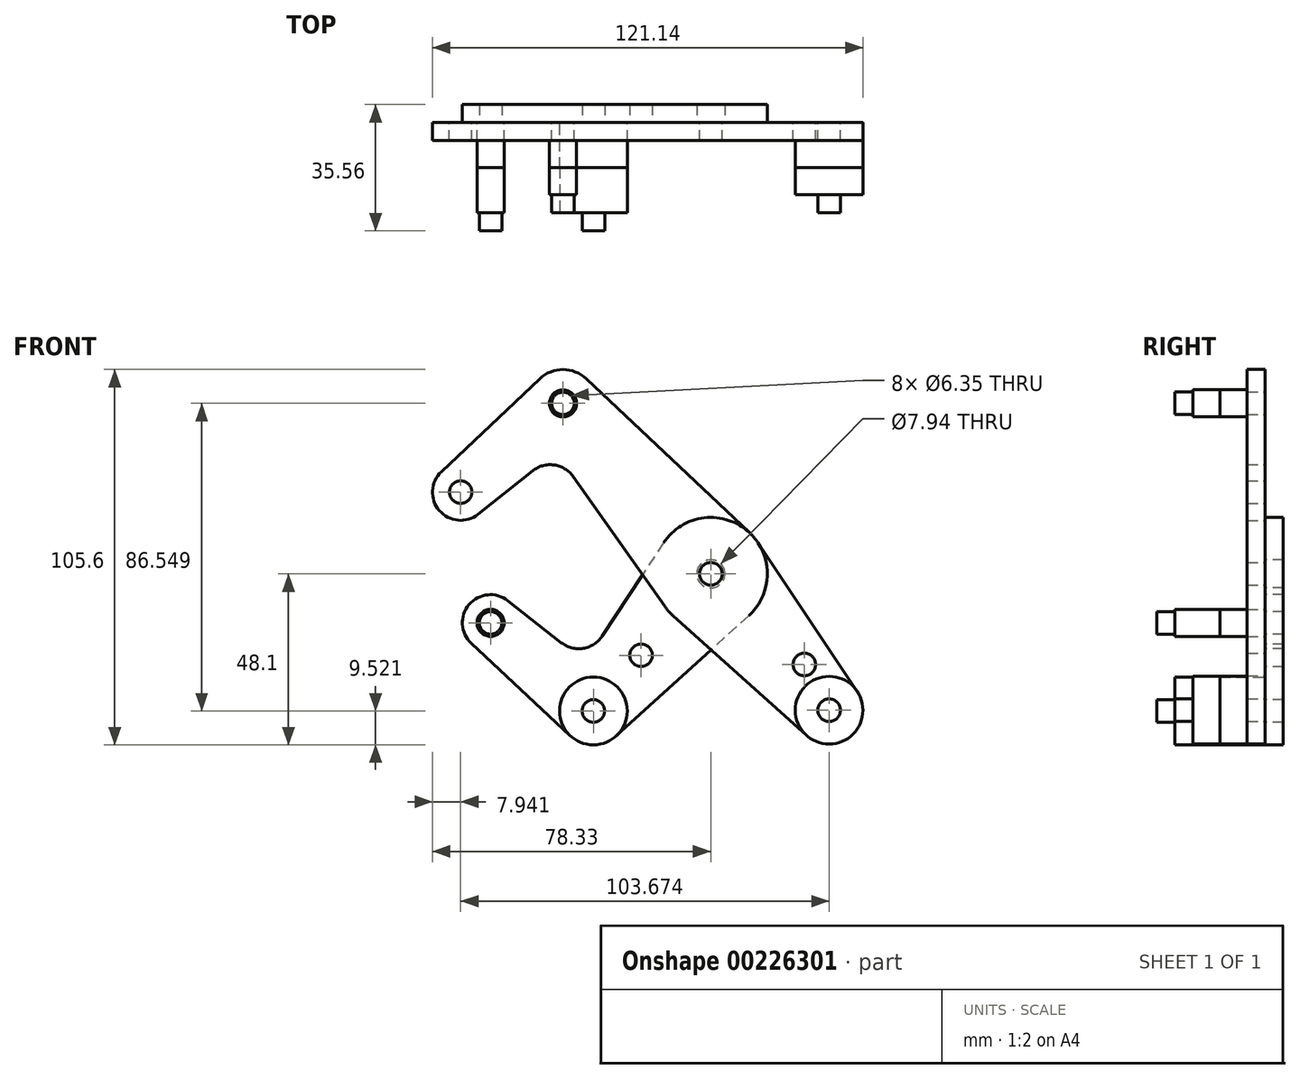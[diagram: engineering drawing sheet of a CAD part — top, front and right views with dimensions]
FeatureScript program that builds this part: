
annotation { "Feature Type Name" : "Feature", "Feature Type Description" : "" }
export const myFeature = defineFeature(function(context is Context, id is Id, definition is map)
    precondition{}
    {
        {
            var Q0;
            Q0=qCreatedBy(makeId("Front.planeOp"),FACE);
            var sketch = newSketch(context, id + "F0", { "sketchPlane" : qUnion([Q0])});
            skLineSegment(sketch, "E0", {"start": v(-41.6, 47.97) * mm, "end": v(41.6, -47.97) * mm, "construction": true});
            skCircle(sketch, "E1", {"center": v(0, 0) * mm, "radius": 3.18 * mm});
            skCircle(sketch, "E2", {"center": v(33.29, -38.38) * mm, "radius": 3.18 * mm});
            skCircle(sketch, "E3", {"center": v(-41.6, 47.97) * mm, "radius": 3.18 * mm});
            skCircle(sketch, "E4", {"center": v(-70.39, 23) * mm, "radius": 3.18 * mm});
            skLineSegment(sketch, "E5", {"start": v(-41.6, 47.97) * mm, "end": v(-70.39, 23) * mm, "construction": true});
            skCircle(sketch, "E6", {"center": v(33.29, -38.38) * mm, "radius": 9.53 * mm});
            skCircle(sketch, "E7", {"center": v(-70.39, 23) * mm, "radius": 7.94 * mm});
            skCircle(sketch, "E8", {"center": v(-41.6, 47.97) * mm, "radius": 9.53 * mm});
            skLineSegment(sketch, "E9", {"start": v(-75.83, 28.78) * mm, "end": v(-48.14, 54.9) * mm});
            skLineSegment(sketch, "E10", {"start": v(-65.44, 16.8) * mm, "end": v(-50.15, 28.98) * mm});
            skCircle(sketch, "E11", {"center": v(0, 0) * mm, "radius": 15.88 * mm});
            skLineSegment(sketch, "E12", {"start": v(-35.07, 54.9) * mm, "end": v(10.9, 11.55) * mm});
            skLineSegment(sketch, "E13", {"start": v(-38.72, 27.35) * mm, "end": v(-12.97, -9.15) * mm});
            skLineSegment(sketch, "E14", {"start": v(-10.6, -11.82) * mm, "end": v(26.93, -45.47) * mm});
            skLineSegment(sketch, "E15", {"start": v(13.2, 8.82) * mm, "end": v(41.2, -33.08) * mm});
            skArc(sketch, "E16.filletArc", {"start": v(-38.72, 27.35) * mm, "mid": v(-44.08, 30.63) * mm, "end": v(-50.15, 28.98) * mm});
            skLineSegment(sketch, "E17", {"start": v(0, 0) * mm, "end": v(-33.05, -38.58) * mm, "construction": true});
            skLineSegment(sketch, "E18", {"start": v(-33.05, -38.58) * mm, "end": v(-61.98, -13.8) * mm, "construction": true});
            skCircle(sketch, "E19", {"center": v(-61.98, -13.8) * mm, "radius": 3.18 * mm});
            skCircle(sketch, "E20", {"center": v(-33.05, -38.58) * mm, "radius": 3.18 * mm});
            skCircle(sketch, "E21", {"center": v(-61.98, -13.8) * mm, "radius": 7.94 * mm});
            skCircle(sketch, "E22", {"center": v(-33.05, -38.58) * mm, "radius": 9.53 * mm});
            skLineSegment(sketch, "E23", {"start": v(-57.08, -7.55) * mm, "end": v(-42.08, -19.35) * mm});
            skLineSegment(sketch, "E24", {"start": v(-67.4, -19.6) * mm, "end": v(-39.54, -45.55) * mm});
            skLineSegment(sketch, "E25", {"start": v(-13.25, 8.74) * mm, "end": v(-30.55, -17.48) * mm});
            skLineSegment(sketch, "E26", {"start": v(10.67, -11.75) * mm, "end": v(-26.65, -45.63) * mm});
            skArc(sketch, "E27.filletArc", {"start": v(-42.08, -19.35) * mm, "mid": v(-35.9, -20.95) * mm, "end": v(-30.55, -17.48) * mm});
            skCircle(sketch, "E28", {"center": v(-19.62, -22.9) * mm, "radius": 3.18 * mm});
            skCircle(sketch, "E29", {"center": v(26.32, -25.5) * mm, "radius": 3.18 * mm});
            skLineSegment(sketch, "E30", {"start": v(26.32, -25.5) * mm, "end": v(23.92, -27.58) * mm, "construction": true});
            skCircle(sketch, "E31", {"center": v(0, 0) * mm, "radius": 3.97 * mm});
            skSolve(sketch);
        }
        {
            var Q0;
            Q0=qCreatedBy(makeId("Front.planeOp"),FACE);
            cPlane(context, id + "F1", {"entities" : qUnion([Q0]), "cplaneType" : CPlaneType.OFFSET, "offset" : 12.7 * mm, "width" : 254 * mm, "height" : 254 * mm});
        }
        {
            var Q0;
            Q0=makeQuery(id+"F0.imprint","IMPRINT",FACE,{"disambiguationData":[TD([[makeQuery(id+"F0.imprint","IMPRINT",EDGE,{"derivedFrom":sQuery(id+"F0.wireOp",EDGE,"E4")}),-1.0]])]});
            var Q1;
            {var subQ1=sQuery(id+"F0.wireOp",EDGE,"E9");Q1=makeQuery(id+"F0.imprint","IMPRINT",FACE,{"disambiguationData":[TD([[makeQuery(id+"F0.imprint","IMPRINT",EDGE,{"derivedFrom":subQ1}),-1.0]])]});}
            var Q2;
            Q2=makeQuery(id+"F0.imprint","IMPRINT",FACE,{"disambiguationData":[TD([[makeQuery(id+"F0.imprint","IMPRINT",EDGE,{"derivedFrom":sQuery(id+"F0.wireOp",EDGE,"E3")}),-1.0]])]});
            var Q3;
            Q3=makeQuery(id+"F0.imprint","IMPRINT",FACE,{"disambiguationData":[TD([[makeQuery(id+"F0.imprint","IMPRINT",EDGE,{"derivedFrom":sQuery(id+"F0.wireOp",EDGE,"E31")}),-1.0]])]});
            var Q4;
            {var subQ0=sQuery(id+"F0.wireOp",EDGE,"E13");var subQ1=sQuery(id+"F0.wireOp",EDGE,"E11");var subQ2=makeQuery(id+"F0.imprint","INTERSECT",VERTEX,{"derivedFrom":[subQ1,subQ0]});Q4=makeQuery(id+"F0.imprint","IMPRINT",FACE,{"disambiguationData":[TD([[makeQuery(id+"F0.imprint","IMPRINT",EDGE,{"disambiguationData":[TD([[subQ2,1.0]])],"derivedFrom":subQ1}),-1.0]])]});}
            var Q5;
            {var subQ0=sQuery(id+"F0.wireOp",EDGE,"E14");var subQ1=sQuery(id+"F0.wireOp",EDGE,"E11");var subQ2=makeQuery(id+"F0.imprint","INTERSECT",VERTEX,{"derivedFrom":[subQ1,subQ0]});Q5=makeQuery(id+"F0.imprint","IMPRINT",FACE,{"disambiguationData":[TD([[makeQuery(id+"F0.imprint","IMPRINT",EDGE,{"disambiguationData":[TD([[subQ2,-1.0]])],"derivedFrom":subQ1}),-1.0]])]});}
            var Q6;
            {var subQ0=sQuery(id+"F0.wireOp",EDGE,"E15");Q6=makeQuery(id+"F0.imprint","IMPRINT",FACE,{"disambiguationData":[TD([[makeQuery(id+"F0.imprint","IMPRINT",EDGE,{"derivedFrom":subQ0}),-1.0]])]});}
            var Q7;
            Q7=makeQuery(id+"F0.imprint","IMPRINT",FACE,{"disambiguationData":[TD([[makeQuery(id+"F0.imprint","IMPRINT",EDGE,{"derivedFrom":sQuery(id+"F0.wireOp",EDGE,"E2")}),-1.0]])]});
            var Q8;
            Q8=makeQuery(id+"F0.imprint","IMPRINT",FACE,{"disambiguationData":[TD([[makeQuery(id+"F0.imprint","IMPRINT",EDGE,{"derivedFrom":sQuery(id+"F0.wireOp",EDGE,"E1")}),-1.0]])]});
            extrude(context, id + "F2", {"entities" : qUnion([Q0, Q1, Q2, Q3, Q4, Q5, Q6, Q7, Q8]), "depth" : 5.08 * mm});
        }
        {
            var Q0;
            Q0=makeQuery(id+"F0.imprint","IMPRINT",FACE,{"disambiguationData":[TD([[makeQuery(id+"F0.imprint","IMPRINT",EDGE,{"derivedFrom":sQuery(id+"F0.wireOp",EDGE,"E31")}),-1.0]])]});
            var Q1;
            {var subQ0=sQuery(id+"F0.wireOp",EDGE,"E14");var subQ1=sQuery(id+"F0.wireOp",EDGE,"E11");var subQ2=makeQuery(id+"F0.imprint","INTERSECT",VERTEX,{"derivedFrom":[subQ1,subQ0]});Q1=makeQuery(id+"F0.imprint","IMPRINT",FACE,{"disambiguationData":[TD([[makeQuery(id+"F0.imprint","IMPRINT",EDGE,{"disambiguationData":[TD([[subQ2,-1.0]])],"derivedFrom":subQ1}),-1.0]])]});}
            var Q2;
            {var subQ10=sQuery(id+"F0.wireOp",EDGE,"E23");Q2=makeQuery(id+"F0.imprint","IMPRINT",FACE,{"disambiguationData":[TD([[makeQuery(id+"F0.imprint","IMPRINT",EDGE,{"derivedFrom":subQ10}),-1.0]])]});}
            var Q3;
            {var subQ0=sQuery(id+"F0.wireOp",EDGE,"E13");var subQ1=sQuery(id+"F0.wireOp",EDGE,"E11");var subQ2=makeQuery(id+"F0.imprint","INTERSECT",VERTEX,{"derivedFrom":[subQ1,subQ0]});Q3=makeQuery(id+"F0.imprint","IMPRINT",FACE,{"disambiguationData":[TD([[makeQuery(id+"F0.imprint","IMPRINT",EDGE,{"disambiguationData":[TD([[subQ2,1.0]])],"derivedFrom":subQ1}),-1.0]])]});}
            var Q4;
            Q4=makeQuery(id+"F0.imprint","IMPRINT",FACE,{"disambiguationData":[TD([[makeQuery(id+"F0.imprint","IMPRINT",EDGE,{"derivedFrom":sQuery(id+"F0.wireOp",EDGE,"E19")}),-1.0]])]});
            var Q5;
            Q5=makeQuery(id+"F0.imprint","IMPRINT",FACE,{"disambiguationData":[TD([[makeQuery(id+"F0.imprint","IMPRINT",EDGE,{"derivedFrom":sQuery(id+"F0.wireOp",EDGE,"E20")}),-1.0]])]});
            extrude(context, id + "F3", {"entities" : qUnion([Q0, Q1, Q2, Q3, Q4, Q5]), "oppositeDirection" : true, "depth" : 5.08 * mm});
        }
        {
            var Q0;
            Q0=makeQuery(id+"F2.opExtrude","CAP_FACE",FACE,{"disambiguationData":[OSD([sQuery(id+"F0.wireOp",EDGE,"E1"),sQuery(id+"F0.wireOp",EDGE,"E2"),sQuery(id+"F0.wireOp",EDGE,"E3"),sQuery(id+"F0.wireOp",EDGE,"E4"),sQuery(id+"F0.wireOp",EDGE,"E6"),sQuery(id+"F0.wireOp",EDGE,"E7"),sQuery(id+"F0.wireOp",EDGE,"E8"),sQuery(id+"F0.wireOp",EDGE,"E9"),sQuery(id+"F0.wireOp",EDGE,"E10"),sQuery(id+"F0.wireOp",EDGE,"E11"),sQuery(id+"F0.wireOp",EDGE,"E12"),sQuery(id+"F0.wireOp",EDGE,"E13"),sQuery(id+"F0.wireOp",EDGE,"E14"),sQuery(id+"F0.wireOp",EDGE,"E15"),sQuery(id+"F0.wireOp",EDGE,"E16.filletArc"),sQuery(id+"F0.wireOp",EDGE,"E29")])],"isStart":true});
            var sketch = newSketch(context, id + "F4", { "sketchPlane" : qUnion([Q0])});
            skCircle(sketch, "E32", {"center": v(41.6, 47.97) * mm, "radius": 3.81 * mm});
            skCircle(sketch, "E33.0", {"center": v(-33.29, -38.38) * mm, "radius": 9.53 * mm});
            skSolve(sketch);
        }
        {
            var Q0;
            Q0=makeQuery(id+"F3.opExtrude","CAP_FACE",FACE,{"disambiguationData":[OSD([sQuery(id+"F0.wireOp",EDGE,"E11"),sQuery(id+"F0.wireOp",EDGE,"E19"),sQuery(id+"F0.wireOp",EDGE,"E20"),sQuery(id+"F0.wireOp",EDGE,"E21"),sQuery(id+"F0.wireOp",EDGE,"E22"),sQuery(id+"F0.wireOp",EDGE,"E23"),sQuery(id+"F0.wireOp",EDGE,"E24"),sQuery(id+"F0.wireOp",EDGE,"E25"),sQuery(id+"F0.wireOp",EDGE,"E26"),sQuery(id+"F0.wireOp",EDGE,"E27.filletArc"),sQuery(id+"F0.wireOp",EDGE,"E28"),sQuery(id+"F0.wireOp",EDGE,"E31")])],"isStart":false});
            var sketch = newSketch(context, id + "F5", { "sketchPlane" : qUnion([Q0])});
            skCircle(sketch, "E34", {"center": v(61.98, -13.8) * mm, "radius": 3.81 * mm});
            skCircle(sketch, "E35.0", {"center": v(33.05, -38.58) * mm, "radius": 9.53 * mm});
            skSolve(sketch);
        }
        {
            var Q0;
            Q0 = qSketchRegion(id + "F4", true);
            var Q1;
            Q1 = qSketchRegion(id + "F5", true);
            var Q2;
            Q2=qCreatedBy(id+"F1.planeOp",FACE);
            extrude(context, id + "F6", {"entities" : qUnion([Q0, Q1]), "endBound" : BoundingType.UP_TO_SURFACE, "oppositeDirection" : true, "endBoundEntityFace" : qUnion([Q2]), "depth" : 25.4 * mm});
        }
        {
            var Q0;
            Q0=makeQuery(id+"F2.opExtrude","SWEPT_BODY",BODY,{"disambiguationData":[OSD([sQuery(id+"F0.wireOp",EDGE,"E1"),sQuery(id+"F0.wireOp",EDGE,"E2"),sQuery(id+"F0.wireOp",EDGE,"E3"),sQuery(id+"F0.wireOp",EDGE,"E4"),sQuery(id+"F0.wireOp",EDGE,"E6"),sQuery(id+"F0.wireOp",EDGE,"E7"),sQuery(id+"F0.wireOp",EDGE,"E8"),sQuery(id+"F0.wireOp",EDGE,"E9"),sQuery(id+"F0.wireOp",EDGE,"E10"),sQuery(id+"F0.wireOp",EDGE,"E11"),sQuery(id+"F0.wireOp",EDGE,"E12"),sQuery(id+"F0.wireOp",EDGE,"E13"),sQuery(id+"F0.wireOp",EDGE,"E14"),sQuery(id+"F0.wireOp",EDGE,"E15"),sQuery(id+"F0.wireOp",EDGE,"E16.filletArc"),sQuery(id+"F0.wireOp",EDGE,"E29")])]});
            var Q1;
            Q1=makeQuery(id+"F3.opExtrude","SWEPT_BODY",BODY,{"disambiguationData":[OSD([sQuery(id+"F0.wireOp",EDGE,"E11"),sQuery(id+"F0.wireOp",EDGE,"E19"),sQuery(id+"F0.wireOp",EDGE,"E20"),sQuery(id+"F0.wireOp",EDGE,"E21"),sQuery(id+"F0.wireOp",EDGE,"E22"),sQuery(id+"F0.wireOp",EDGE,"E23"),sQuery(id+"F0.wireOp",EDGE,"E24"),sQuery(id+"F0.wireOp",EDGE,"E25"),sQuery(id+"F0.wireOp",EDGE,"E26"),sQuery(id+"F0.wireOp",EDGE,"E27.filletArc"),sQuery(id+"F0.wireOp",EDGE,"E28"),sQuery(id+"F0.wireOp",EDGE,"E31")])]});
            var Q2;
            Q2=makeQuery(id+"F6.opExtrude","SWEPT_BODY",BODY,{"disambiguationData":[OSD([sQuery(id+"F4.wireOp",EDGE,"E32")])]});
            var Q3;
            Q3=makeQuery(id+"F6.opExtrude","SWEPT_BODY",BODY,{"disambiguationData":[OSD([sQuery(id+"F5.wireOp",EDGE,"E34")])]});
            var Q4;
            Q4=makeQuery(id+"F6.opExtrude","SWEPT_BODY",BODY,{"disambiguationData":[OSD([sQuery(id+"F5.wireOp",EDGE,"E35.0")])]});
            var Q5;
            Q5=makeQuery(id+"F6.opExtrude","SWEPT_BODY",BODY,{"disambiguationData":[OSD([sQuery(id+"F4.wireOp",EDGE,"E33.0")])]});
            booleanBodies(context, id + "F7", {"operationType" : BooleanOperationType.SUBTRACTION, "tools" : qUnion([Q0, Q1]), "targets" : qUnion([Q2, Q3, Q4, Q5]), "keepTools" : true});
        }
        {
            var Q0;
            Q0=makeQuery(id+"F6.opExtrude","SWEPT_BODY",BODY,{"disambiguationData":[OSD([sQuery(id+"F5.wireOp",EDGE,"E35.0")])]});
            var Q1;
            Q1=makeQuery(id+"F6.opExtrude","SWEPT_BODY",BODY,{"disambiguationData":[OSD([sQuery(id+"F4.wireOp",EDGE,"E32")])]});
            var Q2;
            Q2=makeQuery(id+"F6.opExtrude","SWEPT_BODY",BODY,{"disambiguationData":[OSD([sQuery(id+"F5.wireOp",EDGE,"E34")])]});
            var Q3;
            Q3=makeQuery(id+"F6.opExtrude","SWEPT_BODY",BODY,{"disambiguationData":[OSD([sQuery(id+"F4.wireOp",EDGE,"E33.0")])]});
            var Q4;
            Q4=qCreatedBy(id+"F1.planeOp",FACE);
            mirror(context, id + "F8", {"entities" : qUnion([Q0, Q1, Q2, Q3]), "mirrorPlane" : qUnion([Q4])});
        }
    });
